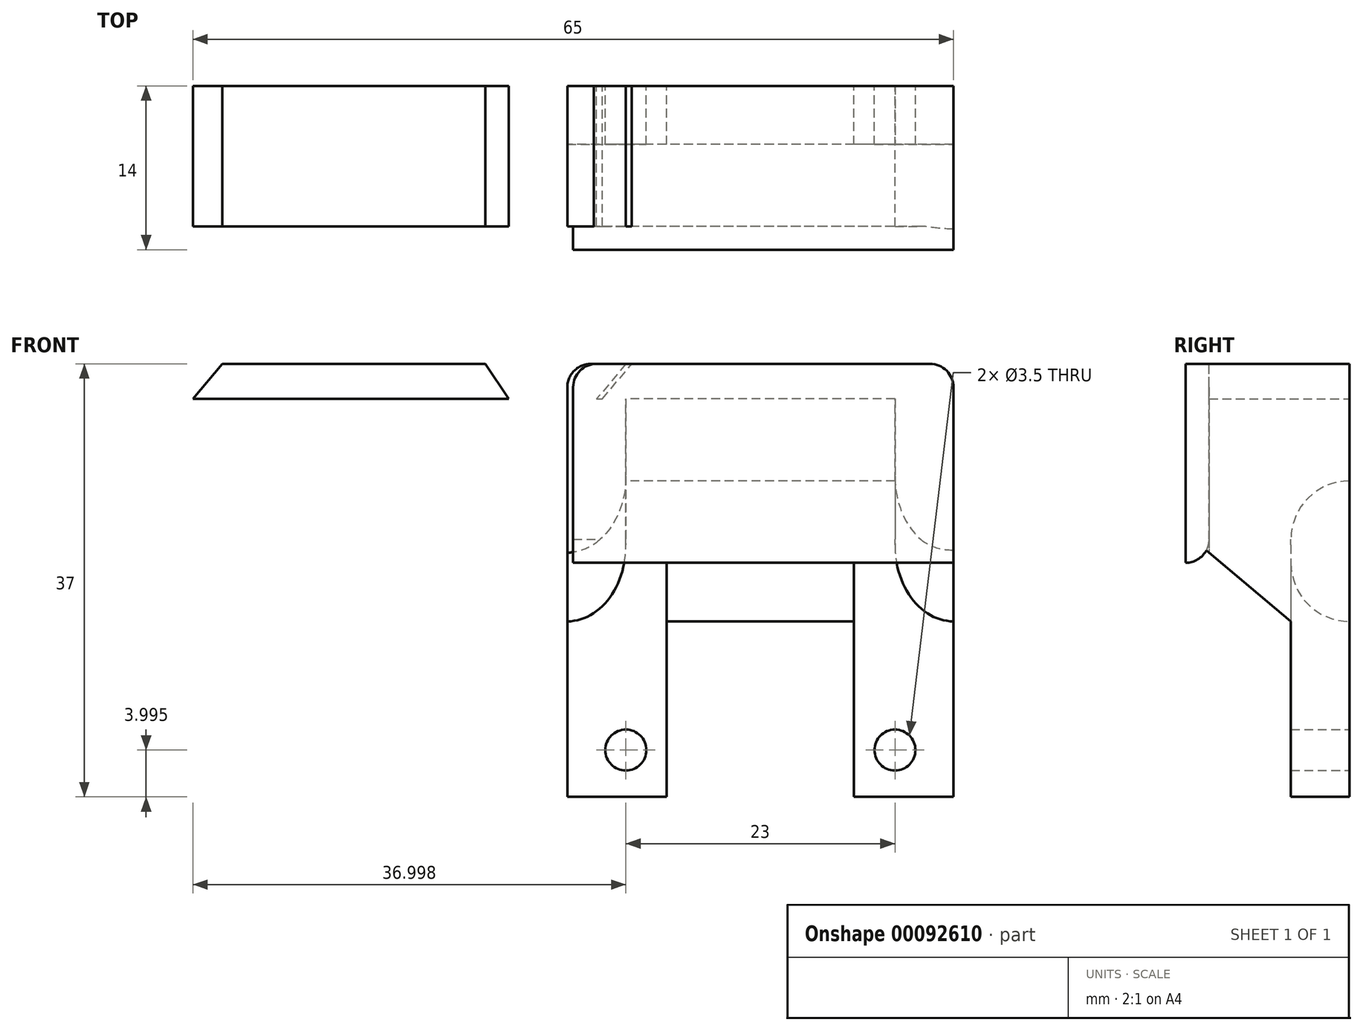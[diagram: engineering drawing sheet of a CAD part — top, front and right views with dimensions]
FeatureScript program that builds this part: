
annotation { "Feature Type Name" : "Feature", "Feature Type Description" : "" }
export const myFeature = defineFeature(function(context is Context, id is Id, definition is map)
    precondition{}
    {
        {
            var Q0;
            Q0=qCreatedBy(makeId("Front.planeOp"),FACE);
            var sketch = newSketch(context, id + "F0", { "sketchPlane" : qUnion([Q0])});
            skLineSegment(sketch, "E0.bottom", {"start": v(-15.76, -1.71) * mm, "end": v(-12.26, -1.71) * mm});
            skLineSegment(sketch, "E0.top", {"start": v(-15.76, 25.29) * mm, "end": v(7.24, 25.29) * mm});
            skLineSegment(sketch, "E0.left", {"start": v(-15.76, -1.71) * mm, "end": v(-15.76, 25.29) * mm, "construction": true});
            skLineSegment(sketch, "E0.right", {"start": v(7.24, -1.71) * mm, "end": v(7.24, 25.29) * mm, "construction": true});
            skCircle(sketch, "E1", {"center": v(-15.76, 2.29) * mm, "radius": 1.75 * mm});
            skCircle(sketch, "E2", {"center": v(7.24, 2.29) * mm, "radius": 1.75 * mm});
            skLineSegment(sketch, "E3.bottom", {"start": v(3.74, 13.29) * mm, "end": v(-12.26, 13.29) * mm});
            skLineSegment(sketch, "E3.left", {"start": v(3.74, 13.29) * mm, "end": v(3.74, -1.71) * mm});
            skLineSegment(sketch, "E3.right", {"start": v(-12.26, 13.29) * mm, "end": v(-12.26, -1.71) * mm});
            skLineSegment(sketch, "E4.bottom", {"start": v(12.24, -1.71) * mm, "end": v(3.74, -1.71) * mm});
            skLineSegment(sketch, "E4.top", {"start": v(12.24, 25.29) * mm, "end": v(-20.76, 25.29) * mm});
            skLineSegment(sketch, "E4.left", {"start": v(12.24, -1.71) * mm, "end": v(12.24, 25.29) * mm});
            skLineSegment(sketch, "E4.right", {"start": v(-20.76, -1.71) * mm, "end": v(-20.76, 25.29) * mm});
            skLineSegment(sketch, "E5.trimOffspring", {"start": v(-12.26, -1.71) * mm, "end": v(-20.76, -1.71) * mm});
            skLineSegment(sketch, "E6.trimOffspring", {"start": v(3.74, -1.71) * mm, "end": v(7.24, -1.71) * mm});
            skSolve(sketch);
        }
        {
            var Q0;
            Q0=makeQuery(id+"F0.imprint","IMPRINT",FACE,{"disambiguationData":[TD([[makeQuery(id+"F0.imprint","IMPRINT",EDGE,{"derivedFrom":sQuery(id+"F0.wireOp",EDGE,"E1")}),-1.0]])]});
            extrude(context, id + "F1", {"entities" : qUnion([Q0]), "depth" : 5 * mm});
        }
        {
            var Q0;
            Q0=makeQuery(id+"F1.opExtrude","SWEPT_FACE",FACE,{"disambiguationData":[OSD([sQuery(id+"F0.wireOp",EDGE,"E4.right")])]});
            var sketch = newSketch(context, id + "F2", { "sketchPlane" : qUnion([Q0])});
            skLineSegment(sketch, "E7", {"start": v(5, 25.29) * mm, "end": v(12, 25.29) * mm});
            skLineSegment(sketch, "E8", {"start": v(12, 25.29) * mm, "end": v(12, 19.16) * mm});
            skLineSegment(sketch, "E9", {"start": v(12, 19.16) * mm, "end": v(5, 13.29) * mm});
            skLineSegment(sketch, "E10.bottom", {"start": v(0, 25.29) * mm, "end": v(12, 25.29) * mm});
            skLineSegment(sketch, "E10.top", {"start": v(0, 35.29) * mm, "end": v(12, 35.29) * mm});
            skLineSegment(sketch, "E10.left", {"start": v(0, 25.29) * mm, "end": v(0, 35.29) * mm});
            skLineSegment(sketch, "E10.right", {"start": v(12, 25.29) * mm, "end": v(12, 35.29) * mm});
            skSolve(sketch);
        }
        {
            var Q0;
            {var subQ0=sQuery(id+"F2.wireOp",EDGE,"E8");Q0=makeQuery(id+"F2.imprint","IMPRINT",FACE,{"disambiguationData":[TD([[makeQuery(id+"F2.imprint","IMPRINT",EDGE,{"derivedFrom":subQ0}),-1.0]])]});}
            var Q1;
            Q1=makeQuery(id+"F2.imprint","IMPRINT",FACE,{"disambiguationData":[TD([[makeQuery(id+"F2.imprint","IMPRINT",EDGE,{"derivedFrom":sQuery(id+"F2.wireOp",EDGE,"E10.top")}),-1.0]])]});
            extrude(context, id + "F3", {"entities" : qUnion([Q0, Q1]), "operationType" : NewBodyOperationType.ADD, "oppositeDirection" : true, "depth" : 5 * mm});
        }
        {
            var Q0;
            Q0=makeQuery(id+"F1.opExtrude","SWEPT_FACE",FACE,{"disambiguationData":[OSD([sQuery(id+"F0.wireOp",EDGE,"E4.left")])]});
            var sketch = newSketch(context, id + "F4", { "sketchPlane" : qUnion([Q0])});
            skLineSegment(sketch, "E11.0", {"start": v(-12, 19.16) * mm, "end": v(-5, 13.29) * mm});
            skLineSegment(sketch, "E11.1", {"start": v(-12, 35.29) * mm, "end": v(-12, 19.16) * mm});
            skLineSegment(sketch, "E11.2", {"start": v(0, 35.29) * mm, "end": v(-12, 35.29) * mm});
            skLineSegment(sketch, "E11.3", {"start": v(0, 25.29) * mm, "end": v(0, 35.29) * mm});
            skSolve(sketch);
        }
        {
            var Q0;
            {var subQ0=sQuery(id+"F4.wireOp",EDGE,"E11.0");Q0=makeQuery(id+"F4.imprint","IMPRINT",FACE,{"disambiguationData":[TD([[makeQuery(id+"F4.imprint","IMPRINT",EDGE,{"derivedFrom":subQ0}),1.0]])]});}
            extrude(context, id + "F5", {"entities" : qUnion([Q0]), "operationType" : NewBodyOperationType.ADD, "oppositeDirection" : true, "depth" : 5 * mm});
        }
        {
            var Q0;
            Q0=makeQuery(id+"F5.boolean.opBoolean","MERGE",FACE,{"derivedFrom":[makeQuery(id+"F3.boolean.opBoolean","MERGE",FACE,{"derivedFrom":[makeQuery(id+"F1.opExtrude","CAP_FACE",FACE,{"disambiguationData":[OSD([sQuery(id+"F0.wireOp",EDGE,"E1"),sQuery(id+"F0.wireOp",EDGE,"E2"),sQuery(id+"F0.wireOp",EDGE,"E3.bottom"),sQuery(id+"F0.wireOp",EDGE,"E3.left"),sQuery(id+"F0.wireOp",EDGE,"E3.right"),sQuery(id+"F0.wireOp",EDGE,"E4.bottom"),sQuery(id+"F0.wireOp",EDGE,"E4.top"),sQuery(id+"F0.wireOp",EDGE,"E4.left"),sQuery(id+"F0.wireOp",EDGE,"E4.right"),sQuery(id+"F0.wireOp",EDGE,"E5.trimOffspring"),sQuery(id+"F0.wireOp",EDGE,"E6.trimOffspring")])],"isStart":true}),makeQuery(id+"F3.opExtrude","SWEPT_FACE",FACE,{"disambiguationData":[OSD([sQuery(id+"F2.wireOp",EDGE,"E10.left")])]})]}),makeQuery(id+"F5.opExtrude","SWEPT_FACE",FACE,{"disambiguationData":[OSD([sQuery(id+"F4.wireOp",EDGE,"E11.3")])]})]});
            var sketch = newSketch(context, id + "F6", { "sketchPlane" : qUnion([Q0])});
            skLineSegment(sketch, "E12", {"start": v(-7.24, 35.29) * mm, "end": v(-9.24, 32.29) * mm});
            skLineSegment(sketch, "E13", {"start": v(-9.24, 32.29) * mm, "end": v(-7.24, 32.29) * mm});
            skLineSegment(sketch, "E14", {"start": v(15.76, 35.29) * mm, "end": v(18.26, 32.29) * mm});
            skPoint(sketch, "E14.endSnap0", {"position": v(18.26, 35.29) * mm});
            skLineSegment(sketch, "E15", {"start": v(18.26, 32.29) * mm, "end": v(15.76, 32.29) * mm});
            skSolve(sketch);
        }
        {
            var Q0;
            {var subQ0=sQuery(id+"F6.wireOp",EDGE,"E12");Q0=makeQuery(id+"F6.imprint","IMPRINT",FACE,{"disambiguationData":[TD([[makeQuery(id+"F6.imprint","IMPRINT",EDGE,{"derivedFrom":subQ0}),1.0]])]});}
            var Q1;
            {var subQ0=sQuery(id+"F6.wireOp",EDGE,"E14");Q1=makeQuery(id+"F6.imprint","IMPRINT",FACE,{"disambiguationData":[TD([[makeQuery(id+"F6.imprint","IMPRINT",EDGE,{"derivedFrom":subQ0}),-1.0]])]});}
            extrude(context, id + "F7", {"entities" : qUnion([Q0, Q1]), "operationType" : NewBodyOperationType.REMOVE, "endBound" : BoundingType.THROUGH_ALL, "oppositeDirection" : true, "depth" : 11 * mm});
        }
        {
            var Q0;
            Q0=makeQuery(id+"F5.boolean.opBoolean","MERGE",FACE,{"derivedFrom":[makeQuery(id+"F3.boolean.opBoolean","MERGE",FACE,{"derivedFrom":[makeQuery(id+"F1.opExtrude","CAP_FACE",FACE,{"disambiguationData":[OSD([sQuery(id+"F0.wireOp",EDGE,"E1"),sQuery(id+"F0.wireOp",EDGE,"E2"),sQuery(id+"F0.wireOp",EDGE,"E3.bottom"),sQuery(id+"F0.wireOp",EDGE,"E3.left"),sQuery(id+"F0.wireOp",EDGE,"E3.right"),sQuery(id+"F0.wireOp",EDGE,"E4.bottom"),sQuery(id+"F0.wireOp",EDGE,"E4.top"),sQuery(id+"F0.wireOp",EDGE,"E4.left"),sQuery(id+"F0.wireOp",EDGE,"E4.right"),sQuery(id+"F0.wireOp",EDGE,"E5.trimOffspring"),sQuery(id+"F0.wireOp",EDGE,"E6.trimOffspring")])],"isStart":true}),makeQuery(id+"F3.opExtrude","SWEPT_FACE",FACE,{"disambiguationData":[OSD([sQuery(id+"F2.wireOp",EDGE,"E10.left")])]})]}),makeQuery(id+"F5.opExtrude","SWEPT_FACE",FACE,{"disambiguationData":[OSD([sQuery(id+"F4.wireOp",EDGE,"E11.3")])]})]});
            var sketch = newSketch(context, id + "F8", { "sketchPlane" : qUnion([Q0])});
            skLineSegment(sketch, "E16", {"start": v(-7.24, 35.29) * mm, "end": v(-9.24, 32.29) * mm});
            skLineSegment(sketch, "E17", {"start": v(-9.24, 32.29) * mm, "end": v(18.26, 32.29) * mm});
            skLineSegment(sketch, "E18", {"start": v(18.26, 32.29) * mm, "end": v(15.76, 35.29) * mm});
            skLineSegment(sketch, "E19", {"start": v(15.76, 35.29) * mm, "end": v(-7.24, 35.29) * mm});
            skLineSegment(sketch, "E20", {"start": v(17.76, 32.29) * mm, "end": v(15.26, 35.29) * mm});
            skSolve(sketch);
        }
        {
            var Q0;
            {var subQ1=sQuery(id+"F8.wireOp",EDGE,"E16");Q0=makeQuery(id+"F8.imprint","IMPRINT",FACE,{"disambiguationData":[TD([[makeQuery(id+"F8.imprint","IMPRINT",EDGE,{"derivedFrom":subQ1}),1.0]])]});}
            var Q1;
            Q1=makeQuery(id+"F7.boolean.opBoolean","COPY",FACE,{"derivedFrom":makeQuery(id+"F7.opExtrude","CAP_FACE",FACE,{"disambiguationData":[OSD([sQuery(id+"F2.wireOp",EDGE,"E10.left"),sQuery(id+"F6.wireOp",EDGE,"E14"),sQuery(id+"F6.wireOp",EDGE,"E15")])],"isStart":false})});
            extrude(context, id + "F9", {"entities" : qUnion([Q0]), "oppositeDirection" : true, "endBoundEntityFace" : qUnion([Q1]), "depth" : 12 * mm});
        }
        {
            var Q0;
            Q0=makeQuery(id+"F1.opExtrude","CAP_EDGE",EDGE,{"disambiguationData":[OSD([sQuery(id+"F0.wireOp",EDGE,"E4.top")])],"isStart":false});
            var Q1;
            Q1=makeQuery(id+"F3.opExtrude","CAP_EDGE",EDGE,{"disambiguationData":[OSD([sQuery(id+"F2.wireOp",EDGE,"E9")])],"isStart":false});
            var Q2;
            Q2=makeQuery(id+"F5.opExtrude","CAP_EDGE",EDGE,{"disambiguationData":[OSD([sQuery(id+"F4.wireOp",EDGE,"E11.0")])],"isStart":false});
            var Q3;
            Q3=makeQuery(id+"F1.opExtrude","CAP_EDGE",EDGE,{"disambiguationData":[OSD([sQuery(id+"F0.wireOp",EDGE,"E3.bottom")])],"isStart":false});
            fillet(context, id + "F10", {"entities" : qUnion([Q0, Q1, Q2, Q3]), "radius" : 5 * mm, "tangentPropagation" : true, "allowEdgeOverflow" : false});
        }
        {
            var Q0;
            Q0=makeQuery(id+"F3.opExtrude","CAP_EDGE",EDGE,{"disambiguationData":[OSD([sQuery(id+"F2.wireOp",EDGE,"E10.top")])],"isStart":true});
            var Q1;
            Q1=makeQuery(id+"F5.opExtrude","CAP_EDGE",EDGE,{"disambiguationData":[OSD([sQuery(id+"F4.wireOp",EDGE,"E11.2")])],"isStart":true});
            fillet(context, id + "F11", {"entities" : qUnion([Q0, Q1]), "radius" : 2 * mm, "tangentPropagation" : true, "allowEdgeOverflow" : false});
        }
        {
            var Q0;
            Q0=makeQuery(id+"F9.opExtrude","SWEPT_BODY",BODY,{"disambiguationData":[OSD([sQuery(id+"F8.wireOp",EDGE,"E16"),sQuery(id+"F8.wireOp",EDGE,"E17"),sQuery(id+"F8.wireOp",EDGE,"E19"),sQuery(id+"F8.wireOp",EDGE,"E20")])]});
            var Q1;
            {var subQ0=sQuery(id+"F0.wireOp",EDGE,"E4.right");Q1=makeQuery(id+"F3.boolean.opBoolean","MERGE",FACE,{"derivedFrom":[makeQuery(id+"F1.opExtrude","SWEPT_FACE",FACE,{"disambiguationData":[OSD([subQ0])]}),makeQuery(id+"F3.opExtrude","CAP_FACE",FACE,{"disambiguationData":[OSD([subQ0,sQuery(id+"F2.wireOp",EDGE,"E8"),sQuery(id+"F2.wireOp",EDGE,"E9"),sQuery(id+"F2.wireOp",EDGE,"E10.bottom"),sQuery(id+"F2.wireOp",EDGE,"E10.top"),sQuery(id+"F2.wireOp",EDGE,"E10.left"),sQuery(id+"F2.wireOp",EDGE,"E10.right")])],"isStart":true})]});}
            transform(context, id + "F12", {"entities" : qUnion([Q0]), "transformType" : TransformType.TRANSLATION_DISTANCE, "transformDirection" : qUnion([Q1]), "distance" : 35 * mm, "makeCopy" : true});
        }
        {
            var Q0;
            Q0=makeQuery(id+"F9.opExtrude","CAP_FACE",FACE,{"disambiguationData":[OSD([sQuery(id+"F8.wireOp",EDGE,"E16"),sQuery(id+"F8.wireOp",EDGE,"E17"),sQuery(id+"F8.wireOp",EDGE,"E19"),sQuery(id+"F8.wireOp",EDGE,"E20")])],"isStart":false});
            var sketch = newSketch(context, id + "F13", { "sketchPlane" : qUnion([Q0])});
            skLineSegment(sketch, "E21", {"start": v(-4.01, 35.29) * mm, "end": v(12.24, 35.29) * mm});
            skPoint(sketch, "E21.endSnap0", {"position": v(-4.01, 35.29) * mm});
            skLineSegment(sketch, "E22", {"start": v(12.24, 35.29) * mm, "end": v(12.24, 18.29) * mm});
            skLineSegment(sketch, "E23", {"start": v(12.24, 18.29) * mm, "end": v(-20.26, 18.29) * mm});
            skLineSegment(sketch, "E24", {"start": v(-20.26, 18.29) * mm, "end": v(-20.26, 35.29) * mm});
            skLineSegment(sketch, "E25", {"start": v(-20.26, 35.29) * mm, "end": v(-4.01, 35.29) * mm});
            skSolve(sketch);
        }
        {
            var Q0;
            {var subQ0=sQuery(id+"F13.wireOp",EDGE,"E22");Q0=makeQuery(id+"F13.imprint","IMPRINT",FACE,{"disambiguationData":[TD([[makeQuery(id+"F13.imprint","IMPRINT",EDGE,{"derivedFrom":subQ0}),-1.0]])]});}
            var Q1;
            {var subQ1=makeQuery(id+"F9.opExtrude","CAP_EDGE",EDGE,{"disambiguationData":[OSD([sQuery(id+"F8.wireOp",EDGE,"E16")])],"isStart":false});Q1=makeQuery(id+"F13.imprint","IMPRINT",FACE,{"disambiguationData":[TD([[makeQuery(id+"F13.imprint","IMPRINT",EDGE,{"derivedFrom":subQ1}),-1.0]])]});}
            extrude(context, id + "F14", {"entities" : qUnion([Q0, Q1]), "operationType" : NewBodyOperationType.ADD, "depth" : 2 * mm});
        }
        {
            var Q0;
            Q0=makeQuery(id+"F14.opExtrude","SWEPT_EDGE",EDGE,{"disambiguationData":[OSD([sQuery(id+"F13.wireOp",EDGE,"E21"),sQuery(id+"F13.wireOp",EDGE,"E22")])]});
            var Q1;
            Q1=makeQuery(id+"F14.opExtrude","SWEPT_EDGE",EDGE,{"disambiguationData":[OSD([sQuery(id+"F13.wireOp",EDGE,"E24"),sQuery(id+"F13.wireOp",EDGE,"E25")])]});
            fillet(context, id + "F15", {"entities" : qUnion([Q0, Q1]), "radius" : 2 * mm, "tangentPropagation" : true, "allowEdgeOverflow" : false});
        }
        {
            var Q0;
            Q0=makeQuery(id+"F14.opExtrude","CAP_EDGE",EDGE,{"disambiguationData":[OSD([sQuery(id+"F13.wireOp",EDGE,"E23")])],"isStart":true});
            fillet(context, id + "F16", {"entities" : qUnion([Q0]), "radius" : 2 * mm, "tangentPropagation" : true, "allowEdgeOverflow" : false});
        }
    });
